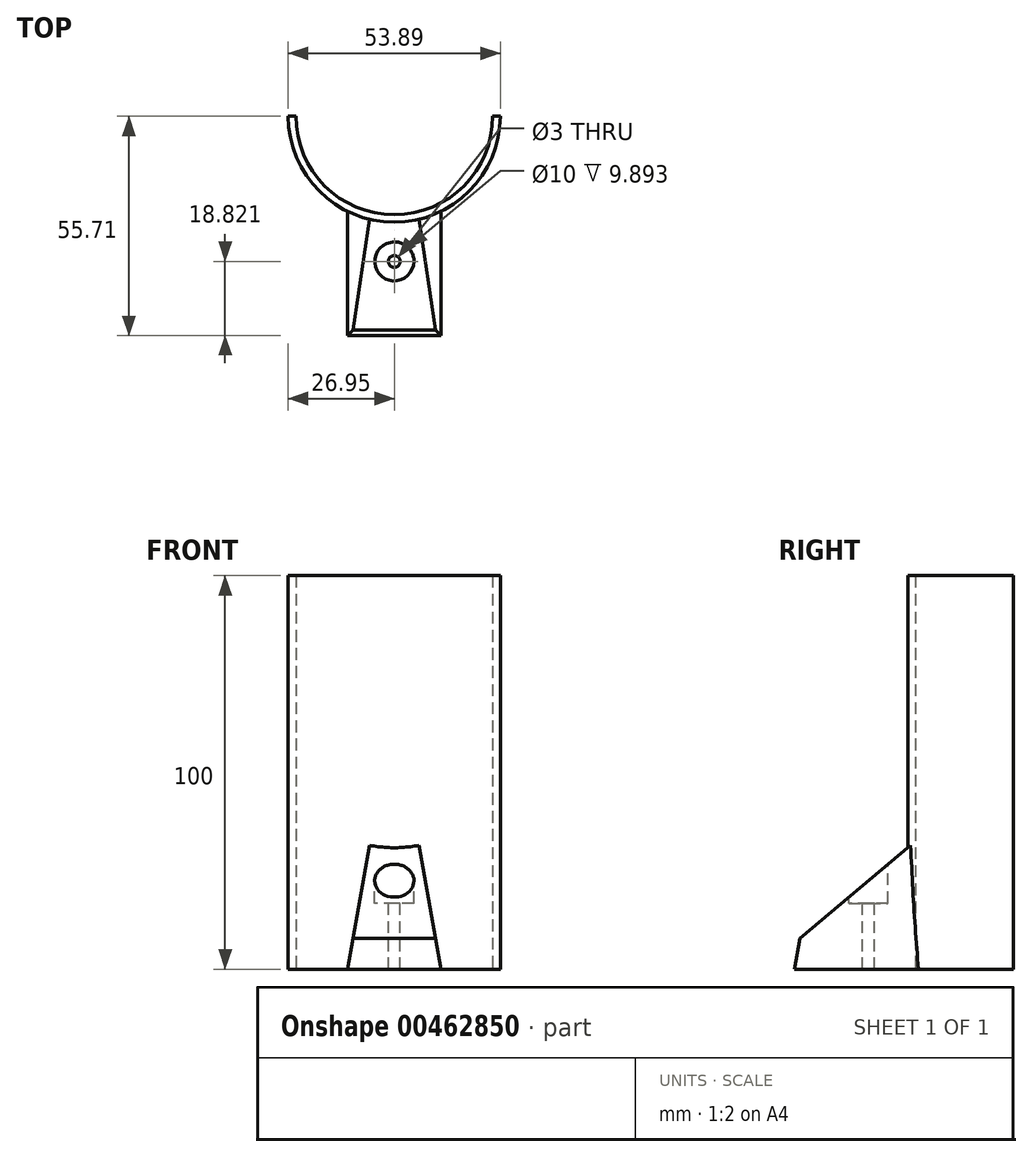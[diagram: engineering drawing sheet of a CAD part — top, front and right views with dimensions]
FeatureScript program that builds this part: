
annotation { "Feature Type Name" : "Feature", "Feature Type Description" : "" }
export const myFeature = defineFeature(function(context is Context, id is Id, definition is map)
    precondition{}
    {
        {
            var Q0;
            Q0=qCreatedBy(makeId("Top.planeOp"),FACE);
            var sketch = newSketch(context, id + "F0", { "sketchPlane" : qUnion([Q0])});
            skLineSegment(sketch, "E0", {"start": v(0, 27) * mm, "end": v(0, -27) * mm, "construction": true});
            skLineSegment(sketch, "E1", {"start": v(27, 0) * mm, "end": v(23.4, 0) * mm, "construction": true});
            skArc(sketch, "E2", {"start": v(-26.95, 0) * mm, "mid": v(0, -26.89) * mm, "end": v(26.94, 0) * mm});
            skLineSegment(sketch, "E3", {"start": v(23.4, 0) * mm, "end": v(-27, 0) * mm, "construction": true});
            skArc(sketch, "E4", {"start": v(-25, 0) * mm, "mid": v(0, -25) * mm, "end": v(25, 0) * mm});
            skLineSegment(sketch, "E5", {"start": v(-26.95, 0) * mm, "end": v(-25, 0) * mm});
            skLineSegment(sketch, "E6", {"start": v(-25, 0) * mm, "end": v(-27, 0) * mm});
            skLineSegment(sketch, "E7", {"start": v(25, 0) * mm, "end": v(27, 0) * mm});
            skLineSegment(sketch, "E8", {"start": v(-27, -52) * mm, "end": v(-25, -52) * mm});
            skLineSegment(sketch, "E9", {"start": v(0, -27) * mm, "end": v(0, -46.89) * mm});
            skLineSegment(sketch, "E10", {"start": v(0, -46.89) * mm, "end": v(-3, -46.89) * mm});
            skLineSegment(sketch, "E11", {"start": v(-3, -46.89) * mm, "end": v(-3, -26.72) * mm});
            skLineSegment(sketch, "E12", {"start": v(0, -46.89) * mm, "end": v(3, -46.89) * mm});
            skLineSegment(sketch, "E13", {"start": v(3, -46.89) * mm, "end": v(3, -26.72) * mm});
            skPoint(sketch, "E14", {"position": v(0, -36.89) * mm});
            skSolve(sketch);
        }
        {
            var Q0;
            {var subQ0=sQuery(id+"F0.wireOp",EDGE,"E7");Q0=makeQuery(id+"F0.imprint","IMPRINT",FACE,{"disambiguationData":[TD([[makeQuery(id+"F0.imprint","IMPRINT",EDGE,{"derivedFrom":subQ0}),-1.0]])]});}
            var Q1;
            {var subQ0=sQuery(id+"F0.wireOp",EDGE,"E5");Q1=makeQuery(id+"F0.imprint","IMPRINT",FACE,{"disambiguationData":[TD([[makeQuery(id+"F0.imprint","IMPRINT",EDGE,{"derivedFrom":subQ0}),-1.0]])]});}
            var Q2;
            {var subQ0=sQuery(id+"F0.wireOp",EDGE,"eb02a1e1-c4c5-46aa-92c9-82ca0152a773");var subQ1=sQuery(id+"F0.wireOp",EDGE,"E2");var subQ2=makeQuery(id+"F0.imprint","INTERSECT",VERTEX,{"disambiguationData":[OD(0.0)],"derivedFrom":[subQ1,subQ0]});Q2=makeQuery(id+"F0.imprint","IMPRINT",FACE,{"disambiguationData":[TD([[makeQuery(id+"F0.imprint","IMPRINT",EDGE,{"disambiguationData":[TD([[subQ2,-1.0]])],"derivedFrom":subQ1}),1.0]])]});}
            extrude(context, id + "F1", {"entities" : qUnion([Q0, Q1, Q2]), "endBound" : BoundingType.SYMMETRIC, "depth" : 100 * mm});
        }
        {
            var Q0;
            Q0=makeQuery(id+"F0.imprint","IMPRINT",FACE,{"disambiguationData":[TD([[makeQuery(id+"F0.imprint","IMPRINT",EDGE,{"derivedFrom":sQuery(id+"F0.wireOp",EDGE,"E10")}),-1.0]])]});
            extrude(context, id + "F2", {"entities" : qUnion([Q0]), "operationType" : NewBodyOperationType.ADD, "oppositeDirection" : true, "depth" : 50 * mm, "hasDraft" : true, "draftAngle" : 10 * degree});
        }
        {
            var Q0;
            Q0=makeQuery(id+"F2.opExtrude","CAP_EDGE",EDGE,{"disambiguationData":[OSD([sQuery(id+"F0.wireOp",EDGE,"E10"),sQuery(id+"F0.wireOp",EDGE,"E12")])],"isStart":true});
            chamfer(context, id + "F3", {"entities" : qUnion([Q0]), "width" : 51 * mm, "tangentPropagation" : true});
        }
        {
            var Q0;
            Q0=sQuery(id+"F0.wireOp",VERTEX,"E14");
            var Q1;
            Q1=makeQuery(id+"F1.opExtrude","SWEPT_BODY",BODY,{"disambiguationData":[OSD([sQuery(id+"F0.wireOp",EDGE,"E2"),sQuery(id+"F0.wireOp",EDGE,"E4"),sQuery(id+"F0.wireOp",EDGE,"E5"),sQuery(id+"F0.wireOp",EDGE,"E7")])]});
            hole(context, id + "F4", {"style" : HoleStyle.C_BORE, "endStyle" : HoleEndStyle.BLIND, "holeDiameter" : 3 * mm, "cBoreDiameter" : 10 * mm, "cBoreDepth" : 1.5 * mm, "holeDepth" : 50 * mm, "isTappedThrough" : true, "tappedDepth" : 12 * mm, "tapClearance" : 3, "locations" : qUnion([Q0]), "scope" : qUnion([Q1])});
        }
        {
            var Q0;
            Q0=sQuery(id+"F0.wireOp",VERTEX,"E4.center");
            var Q1;
            Q1=makeQuery(id+"F1.opExtrude","SWEPT_BODY",BODY,{"disambiguationData":[OSD([sQuery(id+"F0.wireOp",EDGE,"E2"),sQuery(id+"F0.wireOp",EDGE,"E4"),sQuery(id+"F0.wireOp",EDGE,"E5"),sQuery(id+"F0.wireOp",EDGE,"E7")])]});
            hole(context, id + "F5", {"style" : HoleStyle.SIMPLE, "endStyle" : HoleEndStyle.BLIND, "holeDiameter" : 50 * mm, "holeDepth" : 50 * mm, "isTappedThrough" : true, "tappedDepth" : 12 * mm, "tapClearance" : 3, "locations" : qUnion([Q0]), "scope" : qUnion([Q1])});
        }
    });
